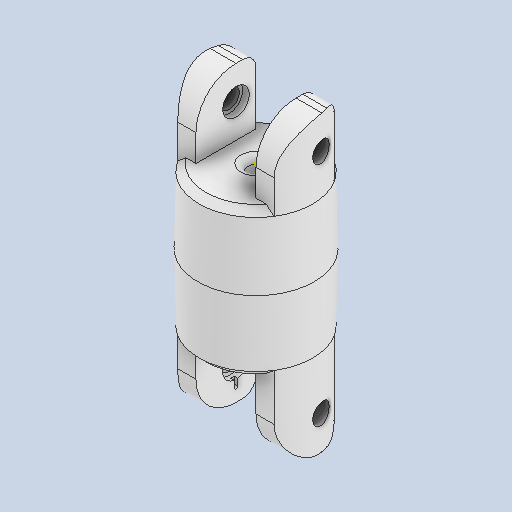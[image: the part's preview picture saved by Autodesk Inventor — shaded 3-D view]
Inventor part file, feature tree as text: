
AUTODESK INVENTOR PART (.ipt)
format: ipt  version: 2022 (Build 260153000, 153)  size: 324,608 bytes
history: native  units: in
note: dims shown in document units (in); Inventor stores cm internally (conversion verified against a paired STEP export)
features: sketch x15, extrude x10, fillet x6, hole x4, chamfer x4, thread x4
ambient origin geometry x8: Origin, YZ Plane, XZ Plane, XY Plane, X Axis, Y Axis, Z Axis, Center Point
bodies: Solid1 (feature_tree)
feature tree (43):
  extrude  "Extrusion1"  Depth=0.6693in
  extrude  "Extrusion2"  Depth=0.0787in TaperAngle=0.0deg
  fillet  "Fillet4"  Radius=0.2362in
  fillet  "Fillet5"  Radius=0.0787in
  hole  "Hole2"  [1 undecoded]
  hole  "Hole3"  [1 undecoded]
  extrude  "Extrusion5"  Depth=0.0197in TaperAngle=0.0deg
  extrude  "Extrusion6"  Depth=0.0394in TaperAngle=45.0deg
  extrude  "Extrusion7"  Depth=0.3937in TaperAngle=0.0deg
  extrude  "Extrusion8"  Depth=0.3937in TaperAngle=45.0deg
  chamfer  "Chamfer3"  Distance=0.3937in
  fillet  "Fillet6"  Radius=0.0394in
  extrude  "Extrusion9"  Depth=0.4331in TaperAngle=45.0deg
  chamfer  "Chamfer4"  Distance=0.1969in
  chamfer  "Chamfer5"  Distance=0.2362in
  fillet  "Fillet7"  Radius=0.2362in
  sketch  "Sketch15"  dims[d99=0.3937in d100=0.0in d101=0.0394in d102=0.4331in d103=45.0deg]
  extrude  "Extrusion12"  Depth=0.2362in TaperAngle=0.0deg
  chamfer  "Chamfer6"  Distance=0.2362in
  fillet  "Fillet8"  Radius=0.0197in
  fillet  "Fillet9"  Radius=0.0344in
  hole  "Hole4"  [1 undecoded]
  hole  "Hole5"  [1 undecoded]
  thread  "Thread1"  [1 undecoded]
  thread  "Thread2"  [1 undecoded]
  thread  "Thread3"  [1 undecoded]
  thread  "Thread4"  [1 undecoded]
  sketch  "Sketch1"  dims[d9=0.4724in d10=0.0in d11=0.6693in]
  sketch  "Sketch2"  dims[d12=0.0984in d13=0.0394in d14=0.0in d28=0.2362in d29=0.0787in]
  sketch  "Sketch4"  dims[d30=0.1969in]
  sketch  "Sketch5"  dims[d31=0.1181in d32=0.2362in d33=0.1575in d34=0.0394in d35=90.0deg d36=0.1575in d37=0.0in d38=0.1969in]
  sketch  "Sketch8"  dims[d39=0.1181in d40=0.2362in d41=0.1575in d42=0.0394in d43=90.0deg d44=0.1575in d45=0.0in d61=0.0197in d62=0.0in]
  sketch  "Sketch9"  dims[d63=0.0197in d64=0.0in d68=0.0197in d69=0.0in]
  sketch  "Sketch10"  dims[d70=0.0197in d71=0.0in d72=0.0394in d73=0.0492in d74=45.0deg]
  sketch  "Sketch11"  dims[d75=0.0394in d77=0.3937in d78=0.0in]
  sketch  "Sketch12"  dims[d79=0.685in d80=0.3937in d81=0.0079in d82=45.0deg d83=0.685in d85=0.0in d86=0.3937in]
  sketch  "Sketch16"  dims[d104=0.2362in]
  sketch  "Sketch17"  dims[d105=0.0787in]
  sketch  "Sketch18"  dims[d106=0.1969in d107=0.1181in d108=0.2362in d109=0.1575in d110=0.0394in d111=90.0deg d112=0.1575in d113=0.0in d114=0.1969in d115=0.1181in d116=0.2362in d117=0.1575in d118=0.0394in d119=90.0deg d120=0.1575in d121=0.0in d122=0.2362in d123=0.0in d124=0.2362in d125=0.0in d126=0.2362in d127=0.0in d128=0.2362in d129=0.0in d50=0.0197in d51=0.0344in d52=0.0197in d53=0.0344in]
  sketch  "Sketch13"  dims[d87=0.0079in d88=0.3937in d89=45.0deg]
  sketch  "Sketch14"  dims[d90=0.0984in d91=0.6693in d93=0.0in d94=0.0394in d95=0.0394in]
  extrude  "Extrusion10"  [1 undecoded]
  extrude  "Extrusion11"  [1 undecoded]
note: 10 required parameter values undecoded (feature->parameter linkage not recoverable at this tier; creation-order binding heuristic only, values carry confidence <= 0.55)
